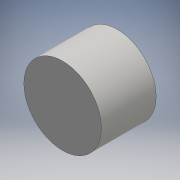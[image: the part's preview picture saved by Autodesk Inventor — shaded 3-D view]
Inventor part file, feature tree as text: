
AUTODESK INVENTOR PART (.ipt)
format: ipt  version: 2016 (Build 200138000, 138)  size: 86,528 bytes
history: native  units: mm
features: extrude x1, sketch x1
ambient origin geometry x8: Origin, YZ Plane, XZ Plane, XY Plane, X Axis, Y Axis, Z Axis, Center Point
bodies: Solid1 (feature_tree)
feature tree (2):
  extrude  "Extrusion1"  Depth=3.0mm TaperAngle=0.0deg
  sketch  "Sketch1"  dims[d0=4.25mm d1=3.0mm d2=0.0mm]
